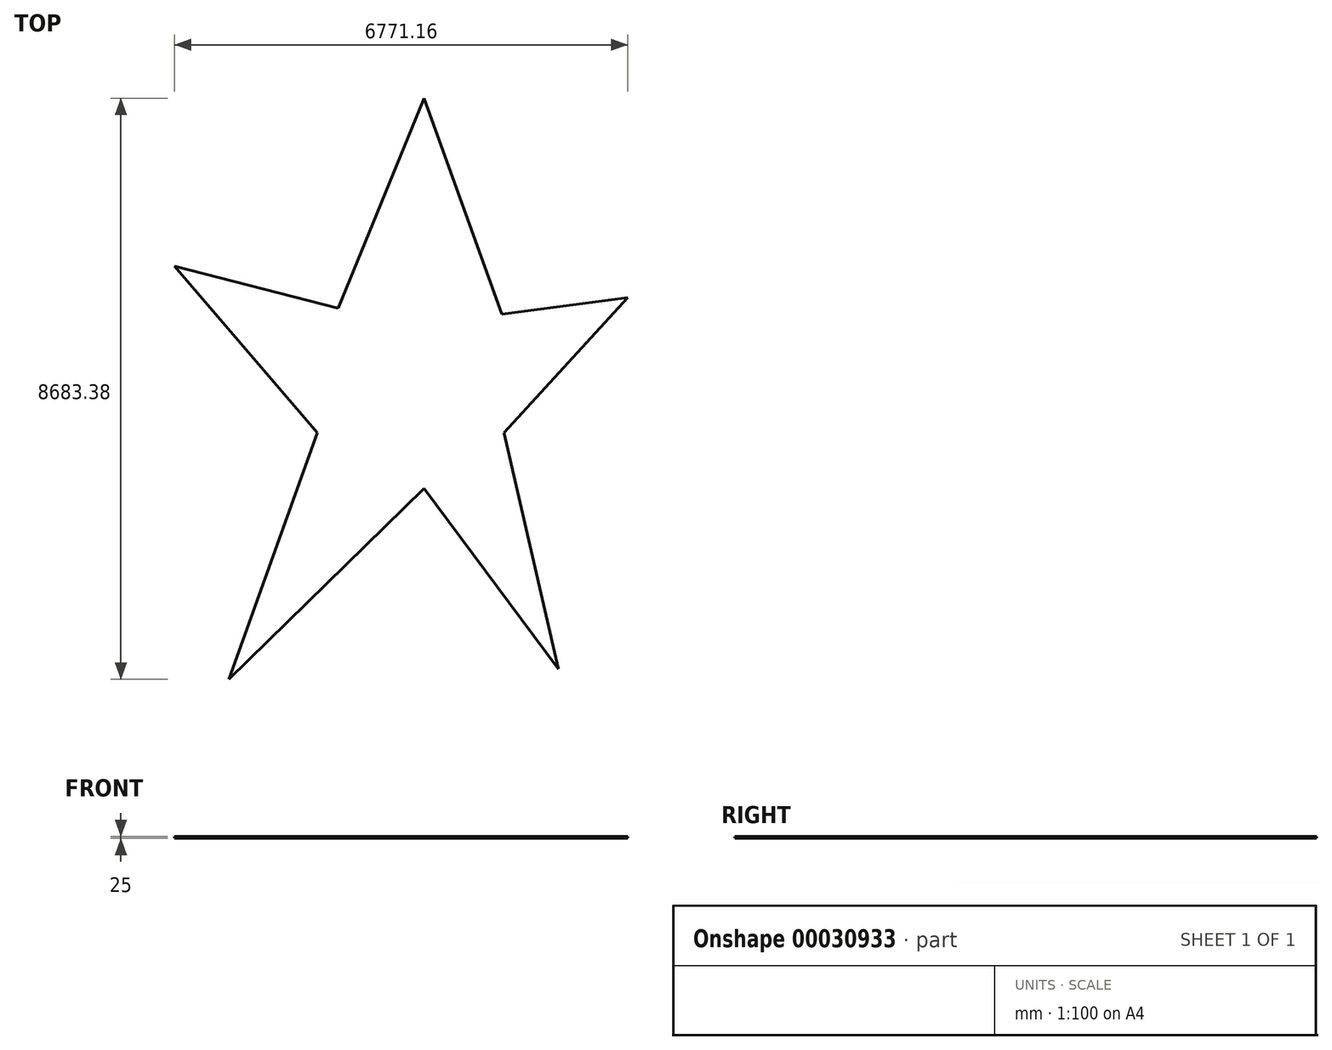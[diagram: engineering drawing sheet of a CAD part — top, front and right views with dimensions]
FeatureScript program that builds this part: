
annotation { "Feature Type Name" : "Feature", "Feature Type Description" : "" }
export const myFeature = defineFeature(function(context is Context, id is Id, definition is map)
    precondition{}
    {
        {
            var Q0;
            Q0=qCreatedBy(makeId("Top.planeOp"),FACE);
            var sketch = newSketch(context, id + "F0", { "sketchPlane" : qUnion([Q0])});
            skLineSegment(sketch, "E0", {"start": v(0, 5000) * mm, "end": v(-1285.27, 1865.2) * mm});
            skLineSegment(sketch, "E1", {"start": v(-1285.27, 1865.2) * mm, "end": v(-3730.4, 2492.16) * mm});
            skLineSegment(sketch, "E2", {"start": v(-3730.4, 2492.16) * mm, "end": v(-1598.75, 0) * mm});
            skLineSegment(sketch, "E3", {"start": v(-1598.75, 0) * mm, "end": v(-2915.36, -3683.38) * mm});
            skLineSegment(sketch, "E4", {"start": v(-2915.36, -3683.38) * mm, "end": v(0, -830.72) * mm});
            skLineSegment(sketch, "E5", {"start": v(0, -830.72) * mm, "end": v(2006.27, -3526.65) * mm});
            skLineSegment(sketch, "E6", {"start": v(2006.27, -3526.65) * mm, "end": v(1191.22, 0) * mm});
            skLineSegment(sketch, "E7", {"start": v(1191.22, 0) * mm, "end": v(3040.75, 2021.94) * mm});
            skLineSegment(sketch, "E8", {"start": v(3040.75, 2021.94) * mm, "end": v(1159.87, 1771.16) * mm});
            skLineSegment(sketch, "E9", {"start": v(1159.87, 1771.16) * mm, "end": v(0, 5000) * mm});
            skSolve(sketch);
        }
        {
            var Q0;
            Q0 = qSketchRegion(id + "F0", true);
            extrude(context, id + "F1", {"entities" : qUnion([Q0]), "depth" : 25 * mm});
        }
    });
